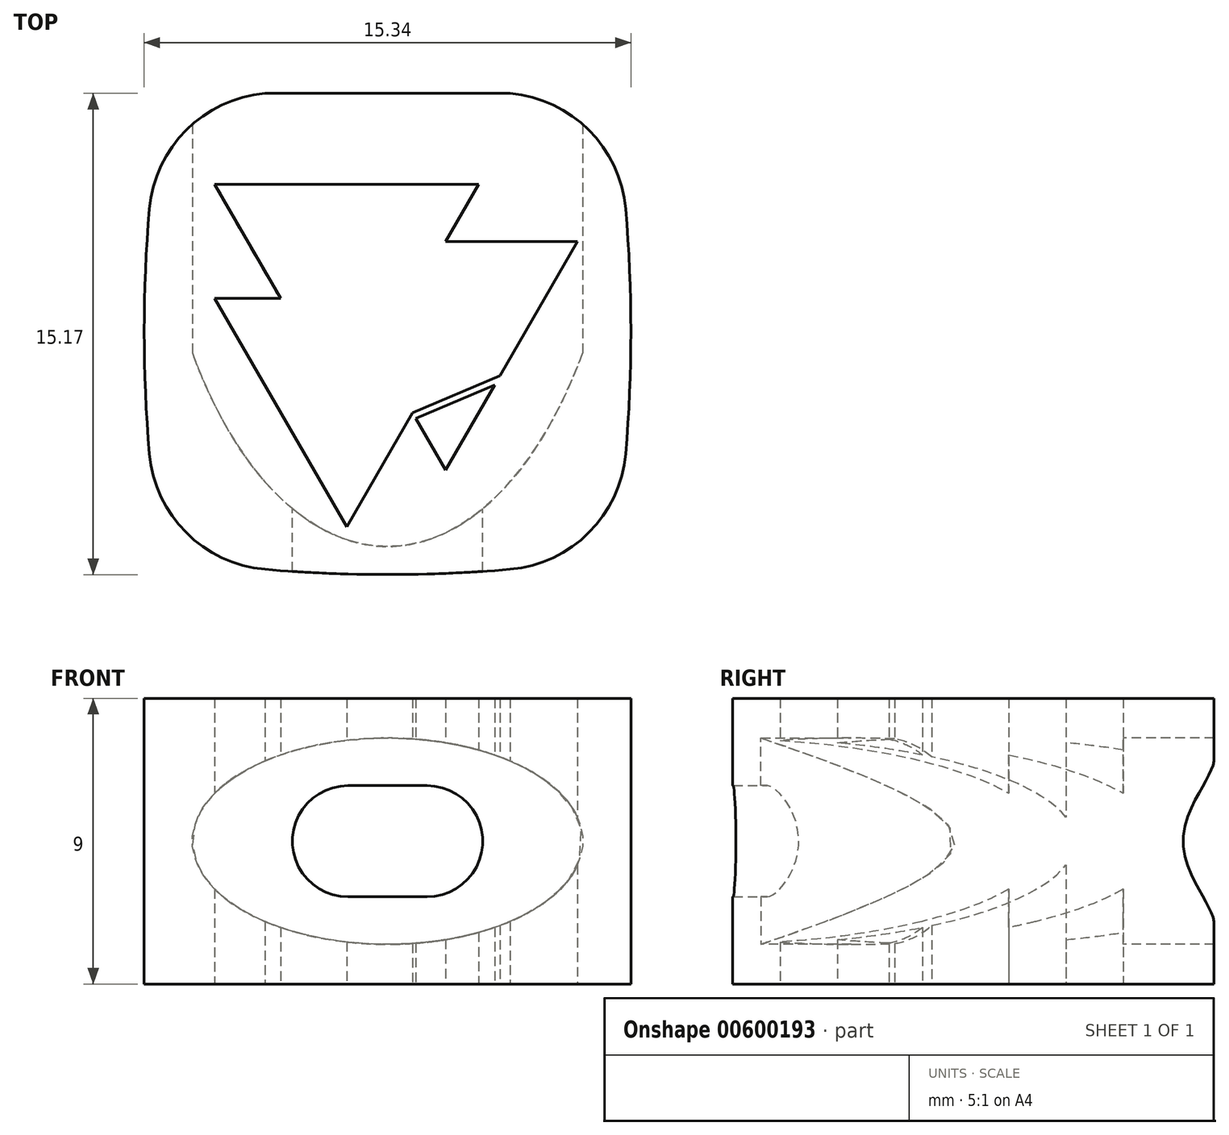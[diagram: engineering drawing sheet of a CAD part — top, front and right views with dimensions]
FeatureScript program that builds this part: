
annotation { "Feature Type Name" : "Feature", "Feature Type Description" : "" }
export const myFeature = defineFeature(function(context is Context, id is Id, definition is map)
    precondition{}
    {
        {
            var Q0;
            Q0=qCreatedBy(makeId("Top.planeOp"),FACE);
            var sketch = newSketch(context, id + "F0", { "sketchPlane" : qUnion([Q0])});
            skArc(sketch, "E0", {"start": v(7.5, -3.86) * mm, "mid": v(7.67, 0) * mm, "end": v(7.5, 3.86) * mm});
            skArc(sketch, "E1", {"start": v(-3.86, -7.5) * mm, "mid": v(0, -7.67) * mm, "end": v(3.86, -7.5) * mm});
            skArc(sketch, "E2", {"start": v(-7.5, 3.86) * mm, "mid": v(-7.67, 0) * mm, "end": v(-7.5, -3.86) * mm});
            skArc(sketch, "E3", {"start": v(3.86, 7.5) * mm, "mid": v(0, 7.67) * mm, "end": v(-3.86, 7.5) * mm});
            skPoint(sketch, "E4.visualSharp", {"position": v(-7.1, -7.1) * mm});
            skArc(sketch, "E4.filletArc", {"start": v(-7.5, -3.86) * mm, "mid": v(-6.34, -6.34) * mm, "end": v(-3.86, -7.5) * mm});
            skPoint(sketch, "E5.visualSharp", {"position": v(7.1, -7.1) * mm});
            skArc(sketch, "E5.filletArc", {"start": v(3.86, -7.5) * mm, "mid": v(6.34, -6.34) * mm, "end": v(7.5, -3.86) * mm});
            skPoint(sketch, "E6.visualSharp", {"position": v(7.1, 7.1) * mm});
            skArc(sketch, "E6.filletArc", {"start": v(7.5, 3.86) * mm, "mid": v(6.34, 6.34) * mm, "end": v(3.86, 7.5) * mm});
            skPoint(sketch, "E7.visualSharp", {"position": v(-7.1, 7.1) * mm});
            skArc(sketch, "E7.filletArc", {"start": v(-3.86, 7.5) * mm, "mid": v(-6.34, 6.34) * mm, "end": v(-7.5, 3.86) * mm});
            skLineSegment(sketch, "E8", {"start": v(-7.1, 7.1) * mm, "end": v(7.1, 7.1) * mm, "construction": true});
            skLineSegment(sketch, "E9", {"start": v(7.1, 7.1) * mm, "end": v(7.1, -7.1) * mm, "construction": true});
            skLineSegment(sketch, "E10", {"start": v(7.1, -7.1) * mm, "end": v(-7.1, -7.1) * mm, "construction": true});
            skLineSegment(sketch, "E11", {"start": v(-7.1, -7.1) * mm, "end": v(-7.1, 7.1) * mm, "construction": true});
            skPoint(sketch, "E12", {"position": v(-7.1, 0) * mm});
            skPoint(sketch, "E13", {"position": v(7.1, 0) * mm});
            skPoint(sketch, "E14", {"position": v(0, 7.1) * mm});
            skPoint(sketch, "E15", {"position": v(0, -7.1) * mm});
            skLineSegment(sketch, "E16", {"start": v(-7.1, 0) * mm, "end": v(7.1, 0) * mm, "construction": true});
            skLineSegment(sketch, "E17", {"start": v(0, 7.1) * mm, "end": v(0, -7.1) * mm, "construction": true});
            skSolve(sketch);
        }
        {
            var Q0;
            Q0=makeQuery(id+"F0.imprint","IMPRINT",FACE,{"disambiguationData":[TD([[makeQuery(id+"F0.imprint","IMPRINT",EDGE,{"derivedFrom":sQuery(id+"F0.wireOp",EDGE,"E0")}),1.0]])]});
            extrude(context, id + "F1", {"entities" : qUnion([Q0]), "depth" : 9 * mm, "offsetDistance" : 25 * mm});
        }
        {
            var Q0;
            Q0=qCreatedBy(makeId("Front.planeOp"),FACE);
            cPlane(context, id + "F2", {"entities" : qUnion([Q0]), "cplaneType" : CPlaneType.OFFSET, "offset" : 9 * mm, "oppositeDirection" : true, "width" : 150 * mm, "height" : 150 * mm});
        }
        {
            var Q0;
            Q0=qCreatedBy(id+"F2.planeOp",FACE);
            var sketch = newSketch(context, id + "F3", { "sketchPlane" : qUnion([Q0])});
            skLineSegment(sketch, "E18", {"start": v(-30.14, 4.5) * mm, "end": v(15.14, 4.5) * mm, "construction": true});
            skLineSegment(sketch, "E19", {"start": v(0, 24.82) * mm, "end": v(0, -6.82) * mm, "construction": true});
            skArc(sketch, "E20", {"start": v(-1.75, 6.25) * mm, "mid": v(-3.5, 4.5) * mm, "end": v(-1.75, 2.75) * mm});
            skArc(sketch, "E21", {"start": v(1.75, 2.75) * mm, "mid": v(3.5, 4.5) * mm, "end": v(1.75, 6.25) * mm});
            skLineSegment(sketch, "E22", {"start": v(-1.75, 6.25) * mm, "end": v(1.75, 6.25) * mm});
            skLineSegment(sketch, "E23", {"start": v(-1.75, 2.75) * mm, "end": v(1.75, 2.75) * mm});
            skSolve(sketch);
        }
        {
            var Q0;
            Q0=makeQuery(id+"F1.opExtrude","CAP_FACE",FACE,{"disambiguationData":[OSD([sQuery(id+"F0.wireOp",EDGE,"E0"),sQuery(id+"F0.wireOp",EDGE,"E1"),sQuery(id+"F0.wireOp",EDGE,"E2"),sQuery(id+"F0.wireOp",EDGE,"E3"),sQuery(id+"F0.wireOp",EDGE,"E4.filletArc"),sQuery(id+"F0.wireOp",EDGE,"E5.filletArc"),sQuery(id+"F0.wireOp",EDGE,"E6.filletArc"),sQuery(id+"F0.wireOp",EDGE,"E7.filletArc")])],"isStart":true});
            var sketch = newSketch(context, id + "F4", { "sketchPlane" : qUnion([Q0])});
            skLineSegment(sketch, "E24", {"start": v(-5.45, -1.03) * mm, "end": v(-1.29, 6.17) * mm});
            skLineSegment(sketch, "E25", {"start": v(-1.29, 6.17) * mm, "end": v(0.79, 2.57) * mm});
            skLineSegment(sketch, "E26", {"start": v(-5.45, -4.63) * mm, "end": v(-3.37, -1.03) * mm});
            skLineSegment(sketch, "E27", {"start": v(2.87, -4.63) * mm, "end": v(-5.45, -4.63) * mm});
            skLineSegment(sketch, "E28", {"start": v(1.83, 4.37) * mm, "end": v(5.99, -2.83) * mm});
            skLineSegment(sketch, "E29", {"start": v(5.99, -2.83) * mm, "end": v(1.83, -2.83) * mm});
            skLineSegment(sketch, "E30.trimOffspring", {"start": v(-3.37, -1.03) * mm, "end": v(-5.45, -1.03) * mm});
            skLineSegment(sketch, "E31.trimOffspring", {"start": v(1.83, -2.83) * mm, "end": v(2.87, -4.63) * mm});
            skLineSegment(sketch, "E32.trimOffspring", {"start": v(0.79, 2.57) * mm, "end": v(1.83, 4.37) * mm});
            skLineSegment(sketch, "E33", {"start": v(-7.52, -4.63) * mm, "end": v(-0.25, 7.97) * mm, "construction": true});
            skLineSegment(sketch, "E34", {"start": v(-0.25, 7.97) * mm, "end": v(7.02, -4.63) * mm, "construction": true});
            skLineSegment(sketch, "E35", {"start": v(7.02, -4.63) * mm, "end": v(-7.52, -4.63) * mm, "construction": true});
            skLineSegment(sketch, "E36", {"start": v(-1.29, 6.17) * mm, "end": v(-7.52, 6.17) * mm, "construction": true});
            skLineSegment(sketch, "E37", {"start": v(-7.52, 6.17) * mm, "end": v(-7.52, 4.37) * mm, "construction": true});
            skPoint(sketch, "E38", {"position": v(-7.52, 4.37) * mm});
            skPoint(sketch, "E39", {"position": v(-7.52, 2.57) * mm});
            skPoint(sketch, "E40", {"position": v(-7.52, 0.77) * mm});
            skPoint(sketch, "E41", {"position": v(-7.52, -1.03) * mm});
            skPoint(sketch, "E42", {"position": v(-7.52, -2.83) * mm});
            skLineSegment(sketch, "E43.trimOffspring", {"start": v(-7.52, 0.77) * mm, "end": v(-7.52, -1.03) * mm, "construction": true});
            skLineSegment(sketch, "E44.trimOffspring", {"start": v(-7.52, -1.03) * mm, "end": v(-7.52, -2.83) * mm, "construction": true});
            skLineSegment(sketch, "E45", {"start": v(-7.52, -4.63) * mm, "end": v(-7.52, -2.83) * mm, "construction": true});
            skLineSegment(sketch, "E46", {"start": v(-7.52, -1.03) * mm, "end": v(-7.52, -1.03) * mm});
            skLineSegment(sketch, "E47", {"start": v(-7.52, 0.77) * mm, "end": v(-7.52, 2.57) * mm, "construction": true});
            skLineSegment(sketch, "E48", {"start": v(-7.52, -2.83) * mm, "end": v(-21.58, -2.83) * mm, "construction": true});
            skLineSegment(sketch, "E49", {"start": v(-7.52, -1.03) * mm, "end": v(-16.59, -1.03) * mm, "construction": true});
            skLineSegment(sketch, "E50", {"start": v(-7.52, 4.37) * mm, "end": v(-19.7, 4.37) * mm, "construction": true});
            skLineSegment(sketch, "E51", {"start": v(-5.45, -1.03) * mm, "end": v(-5.45, -4.63) * mm, "construction": true});
            skLineSegment(sketch, "E52", {"start": v(-1.29, 6.17) * mm, "end": v(-1.29, -4.63) * mm, "construction": true});
            skPoint(sketch, "E52.endSnap0", {"position": v(-1.29, -4.63) * mm});
            skPoint(sketch, "E53", {"position": v(-1.29, 0.77) * mm});
            skLineSegment(sketch, "E54", {"start": v(-0.25, 7.97) * mm, "end": v(-0.25, -4.63) * mm, "construction": true});
            skLineSegment(sketch, "E55", {"start": v(1.83, 4.37) * mm, "end": v(1.83, -4.63) * mm, "construction": true});
            skPoint(sketch, "E56", {"position": v(1.83, -0.13) * mm});
            skLineSegment(sketch, "E57", {"start": v(-7.52, 4.37) * mm, "end": v(-7.52, 2.57) * mm, "construction": true});
            skSolve(sketch);
        }
        {
            var Q0;
            Q0 = qSketchRegion(id + "F4", true);
            extrude(context, id + "F5", {"entities" : qUnion([Q0]), "operationType" : NewBodyOperationType.REMOVE, "endBound" : BoundingType.THROUGH_ALL, "oppositeDirection" : true, "depth" : 25 * mm, "offsetDistance" : 25 * mm});
        }
        {
            var Q0;
            Q0=makeQuery(id+"F1.opExtrude","CAP_FACE",FACE,{"disambiguationData":[OSD([sQuery(id+"F0.wireOp",EDGE,"E0"),sQuery(id+"F0.wireOp",EDGE,"E1"),sQuery(id+"F0.wireOp",EDGE,"E2"),sQuery(id+"F0.wireOp",EDGE,"E3"),sQuery(id+"F0.wireOp",EDGE,"E4.filletArc"),sQuery(id+"F0.wireOp",EDGE,"E5.filletArc"),sQuery(id+"F0.wireOp",EDGE,"E6.filletArc"),sQuery(id+"F0.wireOp",EDGE,"E7.filletArc")])],"isStart":true});
            var sketch = newSketch(context, id + "F6", { "sketchPlane" : qUnion([Q0])});
            skLineSegment(sketch, "E58", {"start": v(0.79, 2.57) * mm, "end": v(3.54, 1.4) * mm});
            skLineSegment(sketch, "E59", {"start": v(3.54, 1.4) * mm, "end": v(3.38, 1.68) * mm});
            skLineSegment(sketch, "E60", {"start": v(3.38, 1.68) * mm, "end": v(0.89, 2.74) * mm});
            skLineSegment(sketch, "E61", {"start": v(0.89, 2.74) * mm, "end": v(0.79, 2.57) * mm});
            skLineSegment(sketch, "E62", {"start": v(3.38, 1.68) * mm, "end": v(3.54, 1.4) * mm});
            skSolve(sketch);
        }
        {
            var Q0;
            Q0 = qSketchRegion(id + "F6", true);
            var Q1;
            Q1=makeQuery(id+"F1.opExtrude","CAP_FACE",FACE,{"disambiguationData":[OSD([sQuery(id+"F0.wireOp",EDGE,"E0"),sQuery(id+"F0.wireOp",EDGE,"E1"),sQuery(id+"F0.wireOp",EDGE,"E2"),sQuery(id+"F0.wireOp",EDGE,"E3"),sQuery(id+"F0.wireOp",EDGE,"E4.filletArc"),sQuery(id+"F0.wireOp",EDGE,"E5.filletArc"),sQuery(id+"F0.wireOp",EDGE,"E6.filletArc"),sQuery(id+"F0.wireOp",EDGE,"E7.filletArc")])],"isStart":false});
            extrude(context, id + "F7", {"entities" : qUnion([Q0]), "operationType" : NewBodyOperationType.ADD, "endBound" : BoundingType.UP_TO_SURFACE, "oppositeDirection" : true, "depth" : 25 * mm, "endBoundEntityFace" : qUnion([Q1]), "offsetDistance" : 25 * mm});
        }
        {
            var Q0;
            Q0=qCreatedBy(makeId("Front.planeOp"),FACE);
            var sketch = newSketch(context, id + "F8", { "sketchPlane" : qUnion([Q0])});
            skLineSegment(sketch, "E63", {"start": v(12.98, 9) * mm, "end": v(-16.2, 9) * mm, "construction": true});
            skLineSegment(sketch, "E64", {"start": v(16.29, 4.5) * mm, "end": v(-18.39, 4.5) * mm, "construction": true});
            skLineSegment(sketch, "E65", {"start": v(0, 0) * mm, "end": v(0, 9) * mm, "construction": true});
            skPoint(sketch, "E66", {"position": v(0, 4.5) * mm});
            skLineSegment(sketch, "E67", {"start": v(1.25, 4.5) * mm, "end": v(-1.25, 4.5) * mm});
            skArc(sketch, "E68.0.startCap", {"start": v(1.25, 6.25) * mm, "mid": v(3, 4.5) * mm, "end": v(1.25, 2.75) * mm});
            skArc(sketch, "E68.0.endCap", {"start": v(-1.25, 2.75) * mm, "mid": v(-3, 4.5) * mm, "end": v(-1.25, 6.25) * mm});
            skLineSegment(sketch, "E68.0.left", {"start": v(1.25, 2.75) * mm, "end": v(-1.25, 2.75) * mm});
            skLineSegment(sketch, "E68.0.right", {"start": v(1.25, 6.25) * mm, "end": v(-1.25, 6.25) * mm});
            skSolve(sketch);
        }
        {
            var Q0;
            Q0 = qSketchRegion(id + "F8", true);
            extrude(context, id + "F9", {"entities" : qUnion([Q0]), "operationType" : NewBodyOperationType.REMOVE, "endBound" : BoundingType.SYMMETRIC, "depth" : 50 * mm, "offsetDistance" : 25 * mm});
        }
        {
            var Q0;
            Q0=makeQuery(id+"F7.boolean.opBoolean","MERGE",FACE,{"derivedFrom":[makeQuery(id+"F1.opExtrude","CAP_FACE",FACE,{"disambiguationData":[OSD([sQuery(id+"F0.wireOp",EDGE,"E0"),sQuery(id+"F0.wireOp",EDGE,"E1"),sQuery(id+"F0.wireOp",EDGE,"E2"),sQuery(id+"F0.wireOp",EDGE,"E3"),sQuery(id+"F0.wireOp",EDGE,"E4.filletArc"),sQuery(id+"F0.wireOp",EDGE,"E5.filletArc"),sQuery(id+"F0.wireOp",EDGE,"E6.filletArc"),sQuery(id+"F0.wireOp",EDGE,"E7.filletArc")])],"isStart":true}),makeQuery(id+"F7.opExtrude","CAP_FACE",FACE,{"disambiguationData":[OSD([sQuery(id+"F6.wireOp",EDGE,"E58"),sQuery(id+"F6.wireOp",EDGE,"E60"),sQuery(id+"F6.wireOp",EDGE,"E61"),sQuery(id+"F6.wireOp",EDGE,"E62")])],"isStart":true})]});
            var sketch = newSketch(context, id + "F10", { "sketchPlane" : qUnion([Q0])});
            skLineSegment(sketch, "E69", {"start": v(-15, -7.5) * mm, "end": v(15, -7.5) * mm});
            skPoint(sketch, "E70", {"position": v(0, -7.5) * mm});
            skLineSegment(sketch, "E71", {"start": v(-15, -7.5) * mm, "end": v(-15, -22.5) * mm});
            skLineSegment(sketch, "E72", {"start": v(-15, -22.5) * mm, "end": v(15, -22.5) * mm});
            skLineSegment(sketch, "E73", {"start": v(15, -22.5) * mm, "end": v(15, -7.5) * mm});
            skSolve(sketch);
        }
        {
            var Q0;
            {var subQ1=makeQuery(id+"F1.opExtrude","CAP_EDGE",EDGE,{"disambiguationData":[OSD([sQuery(id+"F0.wireOp",EDGE,"E3")])],"isStart":true});Q0=makeQuery(id+"F10.imprint","IMPRINT",FACE,{"disambiguationData":[TD([[makeQuery(id+"F10.imprint","IMPRINT",EDGE,{"derivedFrom":subQ1}),-1.0]])]});}
            var Q1;
            {var subQ0=sQuery(id+"F0.wireOp",EDGE,"E7.filletArc");var subQ1=sQuery(id+"F0.wireOp",EDGE,"E6.filletArc");var subQ2=sQuery(id+"F0.wireOp",EDGE,"E5.filletArc");var subQ3=sQuery(id+"F0.wireOp",EDGE,"E4.filletArc");var subQ4=sQuery(id+"F0.wireOp",EDGE,"E3");var subQ5=sQuery(id+"F0.wireOp",EDGE,"E2");var subQ6=sQuery(id+"F0.wireOp",EDGE,"E1");var subQ7=sQuery(id+"F0.wireOp",EDGE,"E0");Q1=makeQuery(id+"F7.boolean.opBoolean","MERGE",FACE,{"derivedFrom":[makeQuery(id+"F1.opExtrude","CAP_FACE",FACE,{"disambiguationData":[OSD([subQ7,subQ6,subQ5,subQ4,subQ3,subQ2,subQ1,subQ0])],"isStart":false}),makeQuery(id+"F7.opExtrude","CAP_FACE",FACE,{"disambiguationData":[OSD([subQ7,subQ6,subQ5,subQ4,subQ3,subQ2,subQ1,subQ0])],"isStart":false})]});}
            extrude(context, id + "F11", {"entities" : qUnion([Q0]), "operationType" : NewBodyOperationType.REMOVE, "endBound" : BoundingType.THROUGH_ALL, "oppositeDirection" : true, "depth" : 25 * mm, "endBoundEntityFace" : qUnion([Q1]), "offsetDistance" : 25 * mm});
        }
        {
            var Q0;
            Q0=makeQuery(id+"F11.boolean.opBoolean","COPY",FACE,{"derivedFrom":makeQuery(id+"F11.opExtrude","SWEPT_FACE",FACE,{"disambiguationData":[OSD([sQuery(id+"F10.wireOp",EDGE,"E69")])]})});
            cPlane(context, id + "F12", {"entities" : qUnion([Q0]), "cplaneType" : CPlaneType.OFFSET, "offset" : 0 * mm, "width" : 150 * mm, "height" : 150 * mm});
        }
        {
            var Q0;
            Q0=qCreatedBy(id+"F12.planeOp",FACE);
            var sketch = newSketch(context, id + "F13", { "sketchPlane" : qUnion([Q0])});
            skLineSegment(sketch, "E74", {"start": v(0, 9) * mm, "end": v(0, 0) * mm, "construction": true});
            skLineSegment(sketch, "E75", {"start": v(-16.9, 9) * mm, "end": v(17.96, 9) * mm, "construction": true});
            skLineSegment(sketch, "E76", {"start": v(15.92, 0) * mm, "end": v(-13.9, 0) * mm, "construction": true});
            skPoint(sketch, "E77", {"position": v(0, 4.5) * mm});
            skLineSegment(sketch, "E78", {"start": v(-14.9, 4.5) * mm, "end": v(17.71, 4.5) * mm, "construction": true});
            skEllipse(sketch, "E79", {"center": v(0, 4.5) * mm, "majorRadius": 6.15 * mm, "minorRadius": 3.25 * mm, "majorAxis": v(1, 0)});
            skSolve(sketch);
        }
        {
            var Q0;
            Q0=qCreatedBy(makeId("Top.planeOp"),FACE);
            var sketch = newSketch(context, id + "F14", { "sketchPlane" : qUnion([Q0])});
            skLineSegment(sketch, "E80", {"start": v(-18.72, 7.5) * mm, "end": v(21.32, 7.5) * mm, "construction": true});
            skLineSegment(sketch, "E81", {"start": v(0, -13.88) * mm, "end": v(0, 19.01) * mm, "construction": true});
            skEllipse(sketch, "E82", {"center": v(0, 7.5) * mm, "majorRadius": 14.28 * mm, "minorRadius": 7.5 * mm, "majorAxis": v(0, -1)});
            skLineSegment(sketch, "E83", {"start": v(-19.44, -6.37) * mm, "end": v(21.42, -6.37) * mm, "construction": true});
            skLineSegment(sketch, "E84", {"start": v(7.5, -12.84) * mm, "end": v(7.5, 15.06) * mm, "construction": true});
            skSolve(sketch);
        }
        {
            var Q0;
            Q0 = qSketchRegion(id + "F13", true);
            extrude(context, id + "F15", {"entities" : qUnion([Q0]), "endBound" : BoundingType.SYMMETRIC, "depth" : 50 * mm, "offsetDistance" : 25 * mm});
        }
        {
            var Q0;
            Q0 = qSketchRegion(id + "F14", true);
            extrude(context, id + "F16", {"entities" : qUnion([Q0]), "endBound" : BoundingType.SYMMETRIC, "depth" : 50 * mm, "offsetDistance" : 25 * mm});
        }
        {
            var Q0;
            Q0=makeQuery(id+"F16.opExtrude","SWEPT_BODY",BODY,{"disambiguationData":[OSD([sQuery(id+"F14.wireOp",EDGE,"E82")])]});
            var Q1;
            Q1=makeQuery(id+"F15.opExtrude","SWEPT_BODY",BODY,{"disambiguationData":[OSD([sQuery(id+"F13.wireOp",EDGE,"E79")])]});
            booleanBodies(context, id + "F17", {"operationType" : BooleanOperationType.INTERSECTION, "tools" : qUnion([Q0, Q1])});
        }
        {
            var Q0;
            Q0=makeQuery(id+"F17.opBoolean","INTERSECT",BODY,{"derivedFrom":[makeQuery(id+"F15.opExtrude","SWEPT_BODY",BODY,{"disambiguationData":[OSD([sQuery(id+"F13.wireOp",EDGE,"E79")])]}),makeQuery(id+"F16.opExtrude","SWEPT_BODY",BODY,{"disambiguationData":[OSD([sQuery(id+"F14.wireOp",EDGE,"E82")])]})]});
            var Q1;
            Q1=makeQuery(id+"F1.opExtrude","SWEPT_BODY",BODY,{"disambiguationData":[OSD([sQuery(id+"F0.wireOp",EDGE,"E0"),sQuery(id+"F0.wireOp",EDGE,"E1"),sQuery(id+"F0.wireOp",EDGE,"E2"),sQuery(id+"F0.wireOp",EDGE,"E3"),sQuery(id+"F0.wireOp",EDGE,"E4.filletArc"),sQuery(id+"F0.wireOp",EDGE,"E5.filletArc"),sQuery(id+"F0.wireOp",EDGE,"E6.filletArc"),sQuery(id+"F0.wireOp",EDGE,"E7.filletArc")])]});
            booleanBodies(context, id + "F18", {"operationType" : BooleanOperationType.SUBTRACTION, "tools" : qUnion([Q0]), "targets" : qUnion([Q1])});
        }
    });
